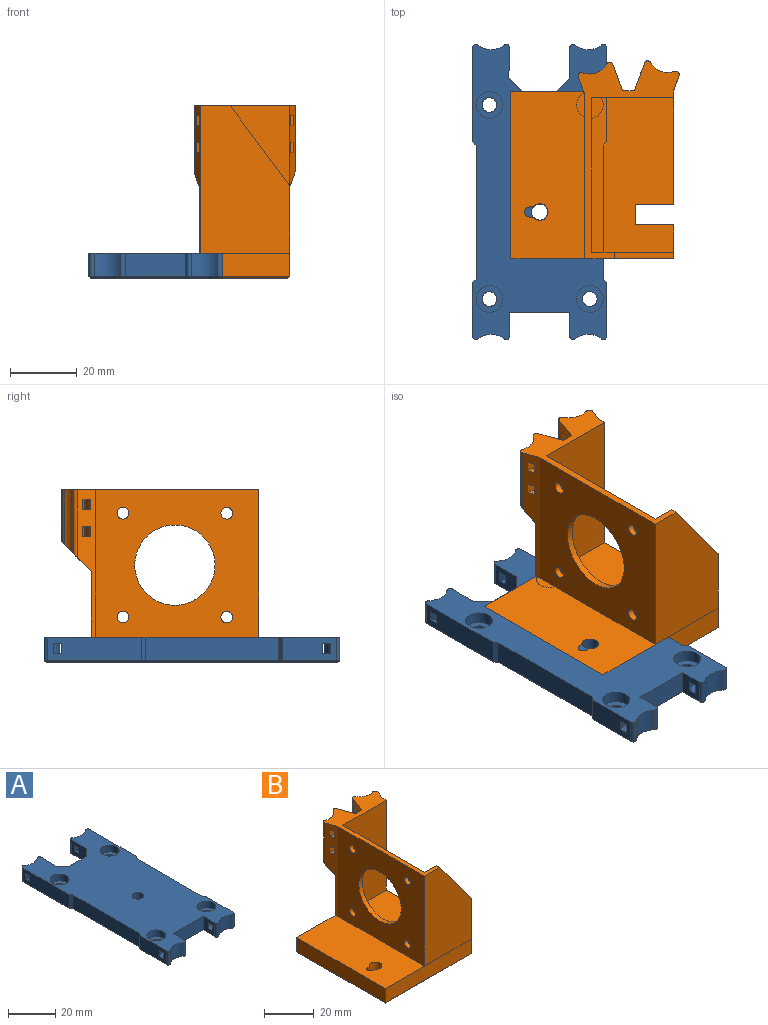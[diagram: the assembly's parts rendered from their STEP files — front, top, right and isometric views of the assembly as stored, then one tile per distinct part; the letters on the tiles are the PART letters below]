
ASSEMBLY  parts=2 mates=1
PART A: 96 faces, bbox 40x88.3x7.5 mm
  f0: cylinder r=2.2mm len=4.4mm, axis (0,0,-1), area 48.4mm2, adj f70,f91
  f1: cylinder r=2.2mm len=4.4mm, axis (0,0,-1), area 48.4mm2, adj f67,f93
  f2: cylinder r=2.2mm len=4.4mm, axis (0,0,-1), area 48.4mm2, adj f68,f95
  f3: cylinder r=2.2mm len=4.4mm, axis (0,0,-1), area 48.4mm2, adj f71,f89
  f4: plane 28.11x7mm, normal (1,0,0), area 189.5mm2, adj f11,f12,f35,f66,f80,f81,f82,f83
  f5: plane 9.11x7mm, normal (-1,0,0), area 56.5mm2, adj f14,f15,f35,f59,f80,f81,f82,f83
  f6: plane 16.14x7mm, normal (-1,0,0), area 105.6mm2, adj f25,f26,f35,f38,f76,f77,f78,f79
  f7: plane 7.14x7mm, normal (1,0,0), area 42.6mm2, adj f28,f29,f35,f46,f76,f77,f78,f79
  f8: plane 16.14x7mm, normal (1,0,0), area 105.6mm2, adj f9,f34,f35,f58,f72,f73,f74,f75
  f9: plane 7x1mm, normal (0.71,0.71,0), area 9.9mm2, adj f8,f10,f35,f60
  f10: plane 40x7mm, normal (1,0,0), area 280mm2, adj f9,f11,f35,f62
  f11: plane 7x1mm, normal (0.71,-0.71,0), area 9.9mm2, adj f4,f10,f35,f64
  f12: cylinder r=1mm len=7mm, axis (0,0,-1), area 15.9mm2, adj f4,f13,f35,f65
  f13: cylinder r=6mm len=7.71mm, axis (0,0,-1), area 58.7mm2, adj f12,f14,f35,f63
  f14: cylinder r=1mm len=7mm, axis (0,0,-1), area 15.9mm2, adj f5,f13,f35,f61
  f15: plane 7x4mm, normal (-0.71,0.71,0), area 39.6mm2, adj f5,f16,f35,f57
  f16: plane 10x7mm, normal (0,1,0), area 70mm2, adj f15,f17,f35,f55
  f17: plane 7x4.2mm, normal (0.71,0.71,0), area 41.6mm2, adj f16,f18,f35,f53
  f18: plane 8.91x7mm, normal (1,-0.02,0), area 55mm2, adj f17,f19,f35,f51,f84,f85,f86,f87
  f19: cylinder r=1mm len=7mm, axis (0,0,-1), area 15.9mm2, adj f18,f20,f35,f49
  f20: cylinder r=6mm len=7.71mm, axis (0,0,-1), area 58.7mm2, adj f19,f21,f35,f47
  f21: cylinder r=1mm len=7mm, axis (0,0,-1), area 15.9mm2, adj f20,f22,f35,f45
  f22: plane 28.11x7mm, normal (-1,0,0), area 189.5mm2, adj f21,f23,f35,f43,f84,f85,f86,f87
  f23: plane 7x1mm, normal (-0.71,-0.71,0), area 9.9mm2, adj f22,f24,f35,f41
  f24: plane 40x7mm, normal (-1,0,0), area 280mm2, adj f23,f25,f35,f39
  f25: plane 7x1mm, normal (-0.71,0.71,0), area 9.9mm2, adj f6,f24,f35,f37
  f26: cylinder r=1mm len=7mm, axis (0,0,-1), area 15.9mm2, adj f6,f27,f35,f40
  f27: cylinder r=6mm len=7.71mm, axis (0,0,-1), area 58.7mm2, adj f26,f28,f35,f42
  f28: cylinder r=1mm len=7mm, axis (0,0,-1), area 15.9mm2, adj f7,f27,f35,f44
  f29: plane 18x7mm, normal (0,-1,0), area 126mm2, adj f7,f30,f35,f48
  f30: plane 7.14x7mm, normal (-1,0,0), area 42.6mm2, adj f29,f31,f35,f50,f72,f73,f74,f75
  f31: cylinder r=1mm len=7mm, axis (0,0,-1), area 15.9mm2, adj f30,f32,f35,f52
  f32: cylinder r=6mm len=7.71mm, axis (0,0,-1), area 58.7mm2, adj f31,f34,f35,f54
  f33: cylinder r=2.4mm len=7mm, axis (0,0,-1), area 105.6mm2, adj f35,f69
  f34: cylinder r=1mm len=7mm, axis (0,0,-1), area 15.9mm2, adj f8,f32,f35,f56
  f35: plane 88.25x40mm, normal (0,0,1), area 2804.5mm2, adj f4,f5,f6,f7,f8,f9,f10,f11
  f36: plane 87.25x39mm, normal (0,0,-1), area 2757.4mm2, adj f37,f38,f39,f40,f41,f42,f43,f44
  f37: plane 1.5x1.21mm, normal (-0.5,0.5,-0.71), area 1mm2, adj f25,f36,f38,f39
  f38: plane 16.14x0.5mm, normal (-0.71,0,-0.71), area 11.3mm2, adj f6,f36,f37,f40
  f39: plane 40.41x0.5mm, normal (-0.71,0,-0.71), area 28.4mm2, adj f24,f36,f37,f41
  f40: cone r=1mm half-angle=45deg, axis (0,0,1), area 1.2mm2, adj f26,f36,f38,f42
  f41: plane 1.5x1.21mm, normal (-0.5,-0.5,-0.71), area 1mm2, adj f23,f36,f39,f43
  f42: cone r=6.5mm half-angle=45deg, axis (0,0,-1), area 6.2mm2, adj f27,f36,f40,f44
  f43: plane 28.11x0.5mm, normal (-0.71,0,-0.71), area 19.8mm2, adj f22,f36,f41,f45
  f44: cone r=1mm half-angle=45deg, axis (0,0,1), area 1.2mm2, adj f28,f36,f42,f46
  f45: cone r=1mm half-angle=45deg, axis (0,0,1), area 1.2mm2, adj f21,f36,f43,f47
  f46: plane 7.64x0.5mm, normal (0.71,0,-0.71), area 5.2mm2, adj f7,f36,f44,f48
  f47: cone r=6.5mm half-angle=45deg, axis (0,0,-1), area 6.2mm2, adj f20,f36,f45,f49
  f48: plane 19x0.5mm, normal (0,-0.71,-0.71), area 13.1mm2, adj f29,f36,f46,f50
  f49: cone r=1mm half-angle=45deg, axis (0,0,1), area 1.2mm2, adj f19,f36,f47,f51
  f50: plane 7.64x0.5mm, normal (-0.71,0,-0.71), area 5.2mm2, adj f30,f36,f48,f52
  f51: plane 9.12x0.71mm, normal (0.71,-0.02,-0.71), area 6.4mm2, adj f18,f36,f49,f53
  f52: cone r=1mm half-angle=45deg, axis (0,0,1), area 1.2mm2, adj f31,f36,f50,f54
  f53: plane 4.7x4.7mm, normal (0.5,0.5,-0.71), area 4.3mm2, adj f17,f36,f51,f55
  f54: cone r=6.5mm half-angle=45deg, axis (0,0,-1), area 6.2mm2, adj f32,f36,f52,f56
  f55: plane 10.41x0.5mm, normal (0,0.71,-0.71), area 7.2mm2, adj f16,f36,f53,f57
  f56: cone r=1mm half-angle=45deg, axis (0,0,1), area 1.2mm2, adj f34,f36,f54,f58
  f57: plane 4.5x4.5mm, normal (-0.5,0.5,-0.71), area 4.1mm2, adj f15,f36,f55,f59
  f58: plane 16.14x0.5mm, normal (0.71,0,-0.71), area 11.3mm2, adj f8,f36,f56,f60
  f59: plane 9.32x0.5mm, normal (-0.71,0,-0.71), area 6.5mm2, adj f5,f36,f57,f61
  f60: plane 1.5x1.21mm, normal (0.5,0.5,-0.71), area 1mm2, adj f9,f36,f58,f62
  f61: cone r=1mm half-angle=45deg, axis (0,0,1), area 1.2mm2, adj f14,f36,f59,f63
  f62: plane 40.41x0.5mm, normal (0.71,0,-0.71), area 28.4mm2, adj f10,f36,f60,f64
  f63: cone r=6.5mm half-angle=45deg, axis (0,0,-1), area 6.2mm2, adj f13,f36,f61,f65
  f64: plane 1.5x1.21mm, normal (0.5,-0.5,-0.71), area 1mm2, adj f11,f36,f62,f66
  f65: cone r=1mm half-angle=45deg, axis (0,0,1), area 1.2mm2, adj f12,f36,f63,f66
  f66: plane 28.11x0.5mm, normal (0.71,0,-0.71), area 19.8mm2, adj f4,f36,f64,f65
  f67: cone r=2.7mm half-angle=45deg, axis (0,0,-1), area 10.9mm2, adj f1,f36
  f68: cone r=2.7mm half-angle=45deg, axis (0,0,-1), area 10.9mm2, adj f2,f36
  f69: cone r=2.9mm half-angle=45deg, axis (0,0,-1), area 11.8mm2, adj f33,f36
  f70: cone r=2.7mm half-angle=45deg, axis (0,0,-1), area 10.9mm2, adj f0,f36
  f71: cone r=2.7mm half-angle=45deg, axis (0,0,-1), area 10.9mm2, adj f3,f36
  f72: plane 11x3.88mm, normal (0,0,-1), area 23.3mm2, adj f8,f30,f73,f75
  f73: cylinder r=9mm len=11mm, axis (0,0,1), area 36.1mm2, adj f8,f30,f72,f74
  f74: plane 11x3.88mm, normal (0,0,1), area 23.3mm2, adj f8,f30,f73,f75
  f75: cylinder r=11mm len=11mm, axis (0,0,1), area 35.1mm2, adj f8,f30,f72,f74
  f76: cylinder r=11mm len=11mm, axis (0,0,1), area 35.1mm2, adj f6,f7,f77,f79
  f77: plane 11x3.88mm, normal (0,0,1), area 23.3mm2, adj f6,f7,f76,f78
  f78: cylinder r=9mm len=11mm, axis (0,0,1), area 36.1mm2, adj f6,f7,f77,f79
  f79: plane 11x3.88mm, normal (0,0,-1), area 23.3mm2, adj f6,f7,f76,f78
  f80: plane 11x3.88mm, normal (0,0,-1), area 23.3mm2, adj f4,f5,f81,f83
  f81: cylinder r=11mm len=11mm, axis (0,0,1), area 35.1mm2, adj f4,f5,f80,f82
  f82: plane 11x3.88mm, normal (0,0,1), area 23.3mm2, adj f4,f5,f81,f83
  f83: cylinder r=9mm len=11mm, axis (0,0,1), area 36.1mm2, adj f4,f5,f80,f82
  f84: cylinder r=11mm len=10.91mm, axis (0,0,1), area 34.8mm2, adj f18,f22,f85,f87
  f85: plane 10.96x3.88mm, normal (0,0,-1), area 23.2mm2, adj f18,f22,f84,f86
  f86: cylinder r=9mm len=10.96mm, axis (0,0,1), area 35.9mm2, adj f18,f22,f85,f87
  f87: plane 10.96x3.88mm, normal (0,0,1), area 23.2mm2, adj f18,f22,f84,f86
  f88: cylinder r=4mm len=8mm, axis (0,0,1), area 88mm2, adj f35,f89
  f89: plane 8x8mm, normal (0,0,1), area 35.1mm2, adj f3,f88
  f90: cylinder r=4mm len=8mm, axis (0,0,1), area 88mm2, adj f35,f91
  f91: plane 8x8mm, normal (0,0,1), area 35.1mm2, adj f0,f90
  f92: cylinder r=4mm len=8mm, axis (0,0,1), area 88mm2, adj f35,f93
  f93: plane 8x8mm, normal (0,0,1), area 35.1mm2, adj f1,f92
  f94: cylinder r=4mm len=8mm, axis (0,0,1), area 88mm2, adj f35,f95
  f95: plane 8x8mm, normal (0,0,1), area 35.1mm2, adj f2,f94
PART B: 67 faces, bbox 52.8x61.6x54 mm
  f0: plane 24.5x4.58mm, normal (0.94,-0.34,0), area 93.1mm2, adj f2,f5,f11,f49,f50,f51,f52,f53
  f1: cylinder r=6mm len=18.53mm, axis (0,0,1), area 137.1mm2, adj f2,f5,f26,f66
  f2: cylinder r=1.05mm len=19.74mm, axis (0,0,1), area 50.8mm2, adj f0,f1,f5,f66
  f3: plane 27.1x10.19mm, normal (1,0,0), area 108.5mm2, adj f4,f13,f14,f18,f22,f31,f39
  f4: plane 44x24.53mm, normal (0,1,0), area 867.7mm2, adj f3,f5,f18,f21,f31
  f5: plane 59.11x30.22mm, normal (0,0,1), area 310.9mm2, adj f0,f1,f2,f4,f6,f11,f20,f21
  f6: plane 51x48.62mm, normal (0,1,0), area 952.3mm2, adj f5,f7,f11,f12,f24,f25,f27,f44
  f7: plane 50.1x22.09mm, normal (0,0,1), area 1081.3mm2, adj f6,f8,f9,f10,f12,f13,f17,f23
  f8: extruded ~7x3mm, area 33mm2, adj f7,f9,f17,f46
  f9: plane 7x1mm, normal (0,-1,0), area 7mm2, adj f7,f8,f10,f45
  f10: cylinder r=2.5mm len=7mm, axis (0,0,-1), area 87.4mm2, adj f7,f9,f17,f47
  f11: plane 51x33.92mm, normal (1,0,0), area 325.4mm2, adj f0,f5,f6,f16,f18,f20,f42
  f12: plane 50.1x7mm, normal (-1,0,0), area 350.7mm2, adj f6,f7,f13,f43
  f13: plane 48.62x7mm, normal (0,-1,0), area 340.3mm2, adj f3,f7,f12,f22,f41
  f14: plane 11.45x7mm, normal (0,1,0), area 80.1mm2, adj f3,f15,f18,f37
  f15: plane 7x6mm, normal (1,0,0), area 42mm2, adj f14,f16,f18,f38
  f16: plane 11.45x7mm, normal (0,-1,0), area 80.1mm2, adj f11,f15,f18,f40
  f17: plane 7x1mm, normal (0,1,0), area 7mm2, adj f7,f8,f10,f48
  f18: plane 46.25x24.53mm, normal (0,0,1), area 1065.8mm2, adj f3,f4,f11,f14,f15,f16,f20,f21
  f19: plane 49.11x47.63mm, normal (0,0,-1), area 2222.5mm2, adj f37,f38,f39,f40,f41,f42,f43,f44
  f20: plane 44x24.53mm, normal (0,-1,0), area 1079.3mm2, adj f5,f11,f18,f21
  f21: plane 46.25x44mm, normal (1,0,0), area 1544.1mm2, adj f4,f5,f18,f20,f32,f33,f34,f35
  f22: plane 44x26.53mm, normal (0,-1,0), area 955.6mm2, adj f3,f5,f13,f23,f31
  f23: plane 48.92x44mm, normal (-1,0,0), area 1661.7mm2, adj f5,f7,f22,f24,f32,f33,f34,f35
  f24: plane 44x5.32mm, normal (-0.94,-0.34,0), area 139.1mm2, adj f5,f6,f7,f23,f28,f57,f58,f59
  f25: plane 24.5x8.35mm, normal (-0.94,0.34,0), area 164.5mm2, adj f5,f6,f26,f49,f50,f51,f52,f53
  f26: cylinder r=1mm len=15.84mm, axis (0,0,1), area 35.8mm2, adj f1,f5,f25,f66
  f27: plane 24.5x7.91mm, normal (0.94,0.34,0), area 157mm2, adj f5,f6,f30,f57,f58,f59,f60,f61
  f28: cylinder r=1mm len=20.2mm, axis (0,0,1), area 44.3mm2, adj f5,f24,f29,f65
  f29: cylinder r=6mm len=19.25mm, axis (0,0,1), area 154.2mm2, adj f5,f28,f30,f65
  f30: cylinder r=1mm len=16.3mm, axis (0,0,1), area 36.8mm2, adj f5,f27,f29,f65
  f31: plane 23.9x17.71mm, normal (0.8,0,0.6), area 55mm2, adj f3,f4,f5,f22
  f32: cylinder r=1.75mm len=3.5mm, axis (1,0,0), area 22mm2, adj f21,f23
  f33: cylinder r=12mm len=24mm, axis (1,0,0), area 150.8mm2, adj f21,f23
  f34: cylinder r=1.75mm len=3.5mm, axis (1,0,0), area 22mm2, adj f21,f23
  f35: cylinder r=1.75mm len=3.5mm, axis (1,0,0), area 22mm2, adj f21,f23
  f36: cylinder r=1.75mm len=3.5mm, axis (1,0,0), area 22mm2, adj f21,f23
  f37: plane 11.95x0.5mm, normal (0,0.71,-0.71), area 8.1mm2, adj f14,f19,f38,f39
  f38: plane 7x0.5mm, normal (0.71,0,-0.71), area 4.6mm2, adj f15,f19,f37,f40
  f39: plane 10.19x0.5mm, normal (0.71,0,-0.71), area 6.8mm2, adj f3,f19,f37,f41
  f40: plane 11.95x0.5mm, normal (0,-0.71,-0.71), area 8.1mm2, adj f16,f19,f38,f42
  f41: plane 48.62x0.5mm, normal (0,-0.71,-0.71), area 34mm2, adj f13,f19,f39,f43
  f42: plane 33.92x0.5mm, normal (0.71,0,-0.71), area 23.6mm2, adj f11,f19,f40,f44
  f43: plane 50.1x0.5mm, normal (-0.71,0,-0.71), area 35.1mm2, adj f12,f19,f41,f44
  f44: plane 48.62x0.5mm, normal (0,0.71,-0.71), area 34mm2, adj f6,f19,f42,f43
  f45: plane 1.02x0.52mm, normal (0,-0.71,-0.71), area 0.6mm2, adj f9,f19,f46,f47
  f46: bspline ~4x2mm, area 3.9mm2, adj f8,f19,f45,f48
  f47: cone r=3mm half-angle=45deg, axis (0,0,-1), area 9.5mm2, adj f10,f19,f45,f48
  f48: plane 1.02x0.52mm, normal (0,0.71,-0.71), area 0.6mm2, adj f17,f19,f46,f47
  f49: cylinder r=9mm len=10.35mm, axis (0,0,-1), area 36.1mm2, adj f0,f25,f50,f52
  f50: plane 11.17x6.19mm, normal (0,0,-1), area 23.4mm2, adj f0,f25,f49,f51
  f51: cylinder r=11.01mm len=10.36mm, axis (0,0,-1), area 35.2mm2, adj f0,f25,f50,f52
  f52: plane 11.17x6.19mm, normal (0,0,1), area 23.4mm2, adj f0,f25,f49,f51
  f53: cylinder r=9mm len=10.35mm, axis (0,0,-1), area 36.1mm2, adj f0,f25,f54,f56
  f54: plane 11.17x6.19mm, normal (0,0,-1), area 23.4mm2, adj f0,f25,f53,f55
  f55: cylinder r=11.01mm len=10.36mm, axis (0,0,-1), area 35.2mm2, adj f0,f25,f54,f56
  f56: plane 11.17x6.19mm, normal (0,0,1), area 23.4mm2, adj f0,f25,f53,f55
  f57: cylinder r=9mm len=10.34mm, axis (0,0,-1), area 36.1mm2, adj f24,f27,f58,f60
  f58: plane 11.16x6.19mm, normal (0,0,-1), area 23.3mm2, adj f24,f27,f57,f59
  f59: cylinder r=11mm len=10.34mm, axis (0,0,-1), area 35.1mm2, adj f24,f27,f58,f60
  f60: plane 11.16x6.19mm, normal (0,0,1), area 23.3mm2, adj f24,f27,f57,f59
  f61: cylinder r=9mm len=10.34mm, axis (0,0,-1), area 36.1mm2, adj f24,f27,f62,f64
  f62: plane 11.16x6.19mm, normal (0,0,-1), area 23.3mm2, adj f24,f27,f61,f63
  f63: cylinder r=11mm len=10.34mm, axis (0,0,-1), area 35.1mm2, adj f24,f27,f62,f64
  f64: plane 11.16x6.19mm, normal (0,0,1), area 23.3mm2, adj f24,f27,f61,f63
  f65: plane 14.47x10.08mm, normal (0,0.72,-0.69), area 103.5mm2, adj f6,f24,f27,f28,f29,f30
  f66: plane 15.91x11.83mm, normal (0,0.72,-0.69), area 111mm2, adj f0,f1,f2,f6,f25,f26
PLACE A rot(axis=(0,-0.29,0.96),0deg) t=(16.16,-3.84,17.36)mm
PLACE B t=(56.18,-23.83,-7.66)mm
MATE slider A.f33 <-> B.f10  axis (0,0,1) through (16.16,-9.83,-0.66)mm
